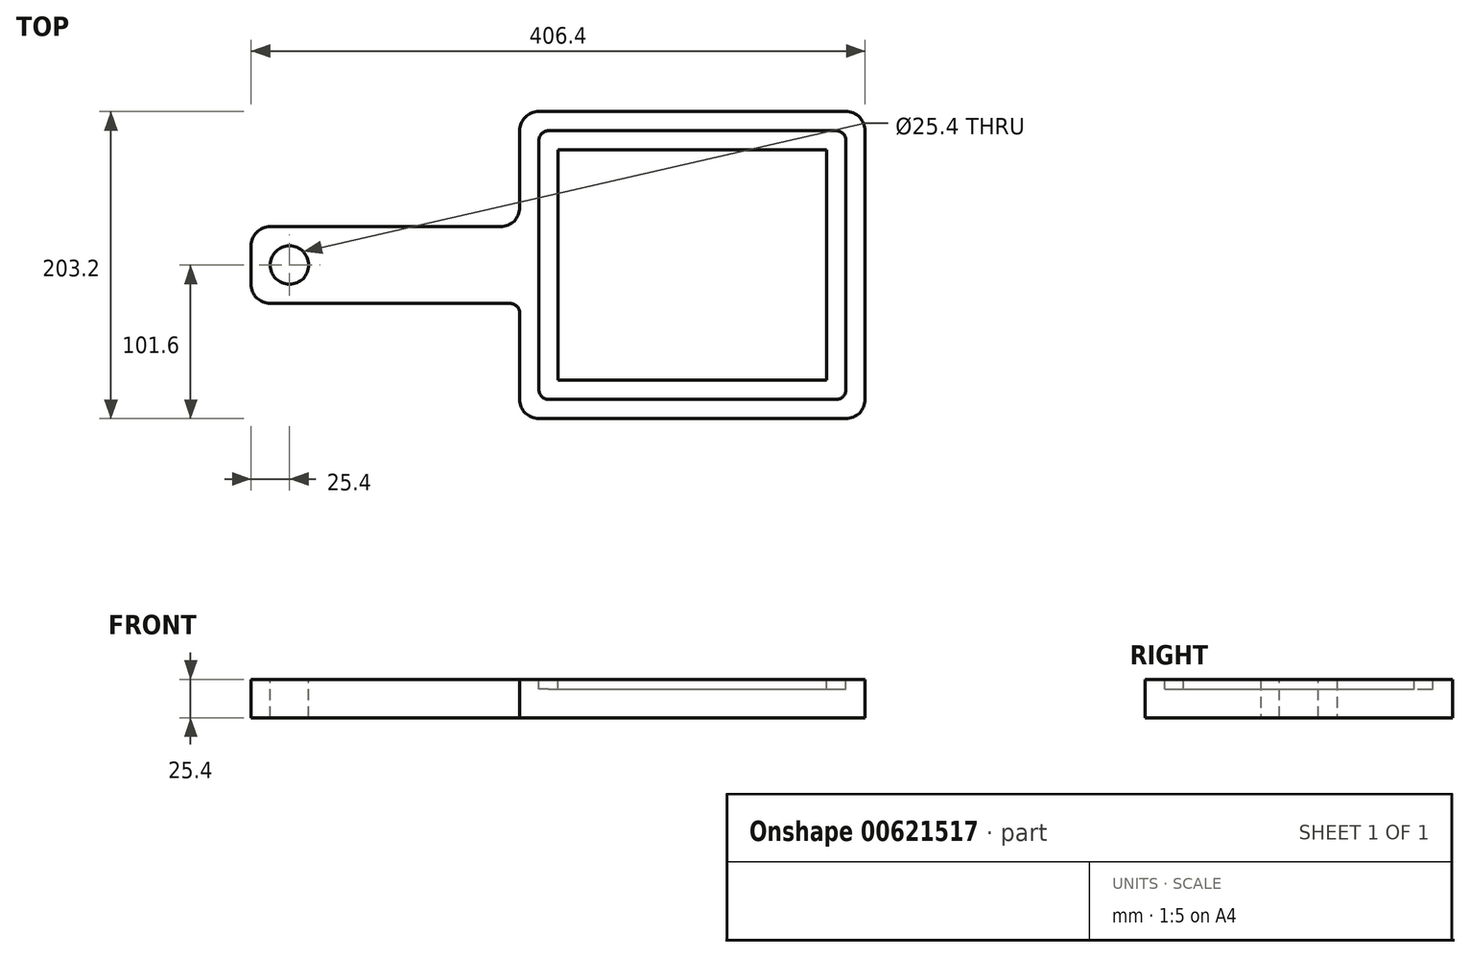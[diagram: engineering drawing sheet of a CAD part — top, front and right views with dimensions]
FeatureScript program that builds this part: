
annotation { "Feature Type Name" : "Feature", "Feature Type Description" : "" }
export const myFeature = defineFeature(function(context is Context, id is Id, definition is map)
    precondition{}
    {
        {
            var Q0;
            Q0=qCreatedBy(makeId("Top.planeOp"),FACE);
            var sketch = newSketch(context, id + "F0", { "sketchPlane" : qUnion([Q0])});
            skLineSegment(sketch, "E0.bottom", {"start": v(0, 0) * mm, "end": v(228.6, 0) * mm});
            skLineSegment(sketch, "E0.top", {"start": v(0, 203.2) * mm, "end": v(228.6, 203.2) * mm});
            skLineSegment(sketch, "E0.left", {"start": v(0, 0) * mm, "end": v(0, 203.2) * mm});
            skLineSegment(sketch, "E0.right", {"start": v(228.6, 0) * mm, "end": v(228.6, 203.2) * mm});
            skLineSegment(sketch, "E1.bottom", {"start": v(0, 127) * mm, "end": v(-177.8, 127) * mm});
            skLineSegment(sketch, "E1.top", {"start": v(0, 76.2) * mm, "end": v(-177.8, 76.2) * mm});
            skLineSegment(sketch, "E1.left", {"start": v(0, 127) * mm, "end": v(0, 76.2) * mm});
            skLineSegment(sketch, "E1.right", {"start": v(-177.8, 127) * mm, "end": v(-177.8, 76.2) * mm});
            skSolve(sketch);
        }
        {
            var Q0;
            Q0=makeQuery(id+"F0.imprint","IMPRINT",FACE,{"disambiguationData":[TD([[makeQuery(id+"F0.imprint","IMPRINT",EDGE,{"derivedFrom":sQuery(id+"F0.wireOp",EDGE,"E1.bottom")}),1.0]])]});
            var Q1;
            {var subQ3=sQuery(id+"F0.wireOp",EDGE,"E0.bottom");Q1=makeQuery(id+"F0.imprint","IMPRINT",FACE,{"disambiguationData":[TD([[makeQuery(id+"F0.imprint","IMPRINT",EDGE,{"derivedFrom":subQ3}),1.0]])]});}
            extrude(context, id + "F1", {"entities" : qUnion([Q0, Q1]), "depth" : 25.4 * mm, "offsetDistance" : 25.4 * mm});
        }
        {
            var Q0;
            Q0=makeQuery(id+"F1.opExtrude","CAP_FACE",FACE,{"disambiguationData":[OSD([sQuery(id+"F0.wireOp",EDGE,"E0.bottom"),sQuery(id+"F0.wireOp",EDGE,"E0.top"),sQuery(id+"F0.wireOp",EDGE,"E0.left"),sQuery(id+"F0.wireOp",EDGE,"E0.right"),sQuery(id+"F0.wireOp",EDGE,"E1.bottom"),sQuery(id+"F0.wireOp",EDGE,"E1.top"),sQuery(id+"F0.wireOp",EDGE,"E1.right")])],"isStart":false});
            var sketch = newSketch(context, id + "F2", { "sketchPlane" : qUnion([Q0])});
            skCircle(sketch, "E2", {"center": v(-152.4, 101.6) * mm, "radius": 12.7 * mm});
            skSolve(sketch);
        }
        {
            var Q0;
            Q0 = qSketchRegion(id + "F2", true);
            extrude(context, id + "F3", {"entities" : qUnion([Q0]), "operationType" : NewBodyOperationType.REMOVE, "oppositeDirection" : true, "depth" : 25.4 * mm, "offsetDistance" : 25.4 * mm});
        }
        {
            var Q0;
            Q0=makeQuery(id+"F1.opExtrude","CAP_FACE",FACE,{"disambiguationData":[OSD([sQuery(id+"F0.wireOp",EDGE,"E0.bottom"),sQuery(id+"F0.wireOp",EDGE,"E0.top"),sQuery(id+"F0.wireOp",EDGE,"E0.left"),sQuery(id+"F0.wireOp",EDGE,"E0.right"),sQuery(id+"F0.wireOp",EDGE,"E1.bottom"),sQuery(id+"F0.wireOp",EDGE,"E1.top"),sQuery(id+"F0.wireOp",EDGE,"E1.right")])],"isStart":false});
            var sketch = newSketch(context, id + "F4", { "sketchPlane" : qUnion([Q0])});
            skLineSegment(sketch, "E3.0", {"start": v(12.7, 12.7) * mm, "end": v(12.7, 76.2) * mm});
            skLineSegment(sketch, "E3.1", {"start": v(12.7, 127) * mm, "end": v(12.7, 190.5) * mm});
            skLineSegment(sketch, "E3.2", {"start": v(12.7, 190.5) * mm, "end": v(215.9, 190.5) * mm});
            skLineSegment(sketch, "E3.3", {"start": v(215.9, 12.7) * mm, "end": v(215.9, 190.5) * mm});
            skLineSegment(sketch, "E3.4", {"start": v(12.7, 12.7) * mm, "end": v(215.9, 12.7) * mm});
            skLineSegment(sketch, "E4", {"start": v(12.7, 127) * mm, "end": v(12.7, 76.2) * mm});
            skLineSegment(sketch, "E5.0", {"start": v(25.4, 127) * mm, "end": v(25.4, 177.8) * mm});
            skLineSegment(sketch, "E5.1", {"start": v(203.2, 25.4) * mm, "end": v(203.2, 177.8) * mm});
            skLineSegment(sketch, "E5.2", {"start": v(25.4, 25.4) * mm, "end": v(203.2, 25.4) * mm});
            skLineSegment(sketch, "E5.3", {"start": v(25.4, 177.8) * mm, "end": v(203.2, 177.8) * mm});
            skLineSegment(sketch, "E5.4", {"start": v(25.4, 25.4) * mm, "end": v(25.4, 76.2) * mm});
            skLineSegment(sketch, "E5.5", {"start": v(25.4, 127) * mm, "end": v(25.4, 76.2) * mm});
            skSolve(sketch);
        }
        {
            var Q0;
            Q0=makeQuery(id+"F4.imprint","IMPRINT",FACE,{"disambiguationData":[TD([[makeQuery(id+"F4.imprint","IMPRINT",EDGE,{"derivedFrom":sQuery(id+"F4.wireOp",EDGE,"E3.0")}),-1.0]])]});
            extrude(context, id + "F5", {"entities" : qUnion([Q0]), "operationType" : NewBodyOperationType.REMOVE, "oppositeDirection" : true, "depth" : 6.35 * mm, "offsetDistance" : 25.4 * mm});
        }
        {
            var Q0;
            Q0=makeQuery(id+"F5.boolean.opBoolean","COPY",EDGE,{"derivedFrom":makeQuery(id+"F5.opExtrude","SWEPT_EDGE",EDGE,{"disambiguationData":[OSD([sQuery(id+"F4.wireOp",EDGE,"E3.1"),sQuery(id+"F4.wireOp",EDGE,"E3.2")])]})});
            var Q1;
            Q1=makeQuery(id+"F5.boolean.opBoolean","COPY",EDGE,{"derivedFrom":makeQuery(id+"F5.opExtrude","SWEPT_EDGE",EDGE,{"disambiguationData":[OSD([sQuery(id+"F4.wireOp",EDGE,"E3.2"),sQuery(id+"F4.wireOp",EDGE,"E3.3")])]})});
            var Q2;
            Q2=makeQuery(id+"F5.boolean.opBoolean","COPY",EDGE,{"derivedFrom":makeQuery(id+"F5.opExtrude","SWEPT_EDGE",EDGE,{"disambiguationData":[OSD([sQuery(id+"F4.wireOp",EDGE,"E3.0"),sQuery(id+"F4.wireOp",EDGE,"E3.4")])]})});
            var Q3;
            Q3=makeQuery(id+"F5.boolean.opBoolean","COPY",EDGE,{"derivedFrom":makeQuery(id+"F5.opExtrude","SWEPT_EDGE",EDGE,{"disambiguationData":[OSD([sQuery(id+"F4.wireOp",EDGE,"E3.3"),sQuery(id+"F4.wireOp",EDGE,"E3.4")])]})});
            fillet(context, id + "F6", {"entities" : qUnion([Q0, Q1, Q2, Q3]), "radius" : 6.35 * mm, "tangentPropagation" : true, "allowEdgeOverflow" : false});
        }
        {
            var Q0;
            Q0=makeQuery(id+"F1.opExtrude","SWEPT_EDGE",EDGE,{"disambiguationData":[OSD([sQuery(id+"F0.wireOp",EDGE,"E0.top"),sQuery(id+"F0.wireOp",EDGE,"E0.left")])]});
            var Q1;
            Q1=makeQuery(id+"F1.opExtrude","SWEPT_EDGE",EDGE,{"disambiguationData":[OSD([sQuery(id+"F0.wireOp",EDGE,"E0.left"),sQuery(id+"F0.wireOp",EDGE,"E1.bottom"),sQuery(id+"F0.wireOp",EDGE,"E1.left")])]});
            var Q2;
            Q2=makeQuery(id+"F1.opExtrude","SWEPT_EDGE",EDGE,{"disambiguationData":[OSD([sQuery(id+"F0.wireOp",EDGE,"E1.bottom"),sQuery(id+"F0.wireOp",EDGE,"E1.right")])]});
            var Q3;
            Q3=makeQuery(id+"F1.opExtrude","SWEPT_EDGE",EDGE,{"disambiguationData":[OSD([sQuery(id+"F0.wireOp",EDGE,"E1.top"),sQuery(id+"F0.wireOp",EDGE,"E1.right")])]});
            var Q4;
            Q4=makeQuery(id+"F1.opExtrude","SWEPT_EDGE",EDGE,{"disambiguationData":[OSD([sQuery(id+"F0.wireOp",EDGE,"E0.top"),sQuery(id+"F0.wireOp",EDGE,"E0.right")])]});
            var Q5;
            Q5=makeQuery(id+"F1.opExtrude","SWEPT_EDGE",EDGE,{"disambiguationData":[OSD([sQuery(id+"F0.wireOp",EDGE,"E0.bottom"),sQuery(id+"F0.wireOp",EDGE,"E0.right")])]});
            var Q6;
            Q6=makeQuery(id+"F1.opExtrude","SWEPT_EDGE",EDGE,{"disambiguationData":[OSD([sQuery(id+"F0.wireOp",EDGE,"E0.bottom"),sQuery(id+"F0.wireOp",EDGE,"E0.left")])]});
            fillet(context, id + "F7", {"entities" : qUnion([Q0, Q1, Q2, Q3, Q4, Q5, Q6]), "radius" : 12.7 * mm, "tangentPropagation" : true, "allowEdgeOverflow" : false});
        }
        {
            var Q0;
            Q0=makeQuery(id+"F1.opExtrude","SWEPT_EDGE",EDGE,{"disambiguationData":[OSD([sQuery(id+"F0.wireOp",EDGE,"E0.left"),sQuery(id+"F0.wireOp",EDGE,"E1.top"),sQuery(id+"F0.wireOp",EDGE,"E1.left")])]});
            fillet(context, id + "F8", {"entities" : qUnion([Q0]), "radius" : 6.35 * mm, "tangentPropagation" : true, "allowEdgeOverflow" : false});
        }
    });
